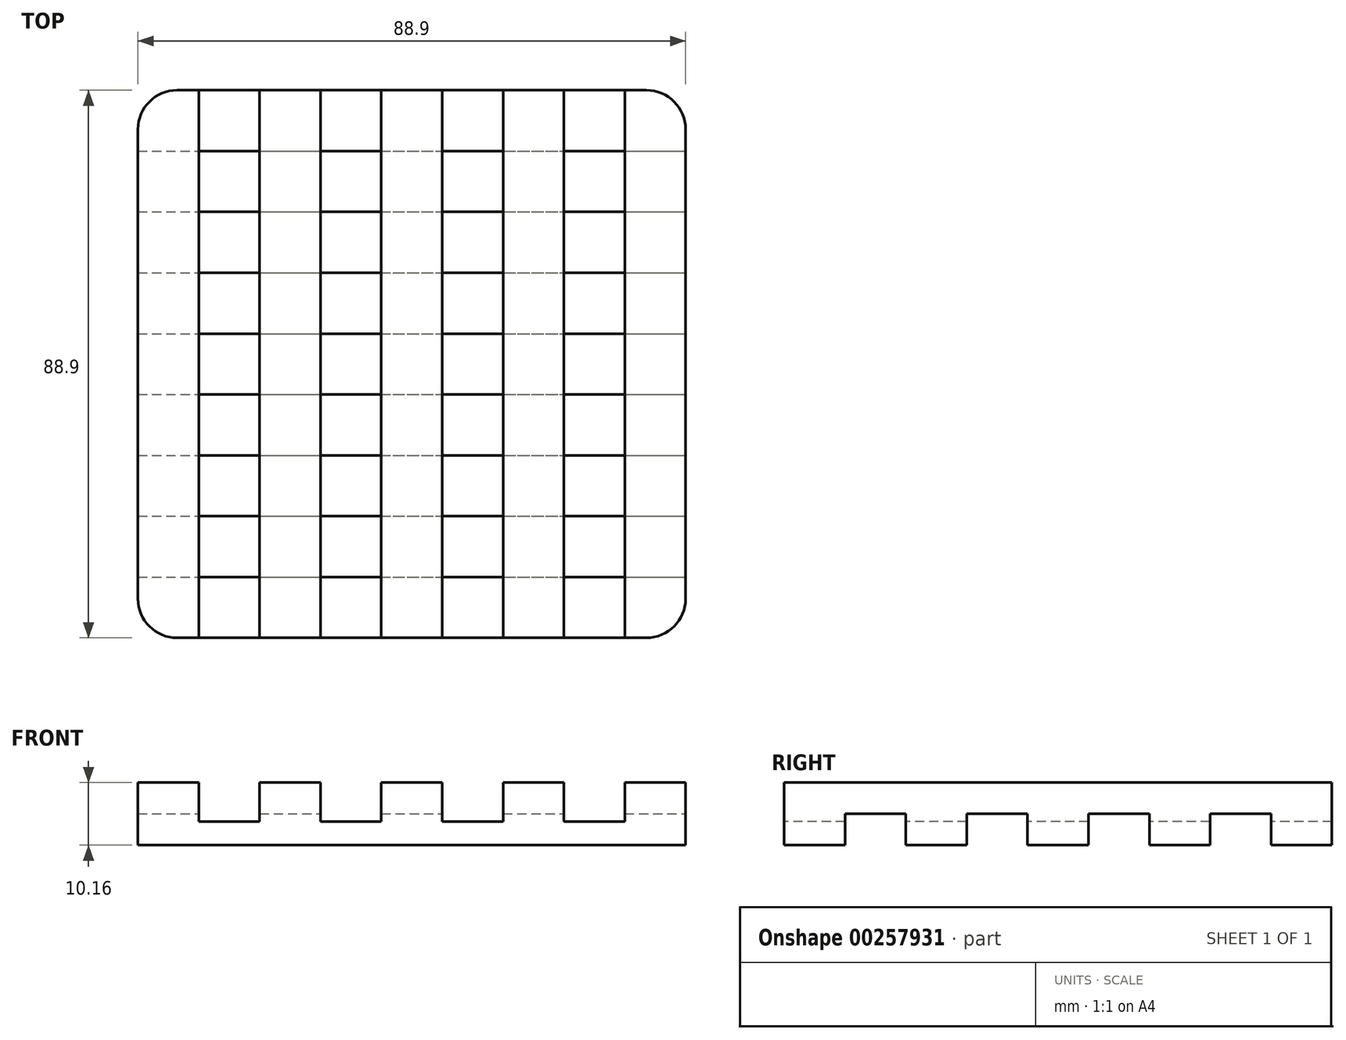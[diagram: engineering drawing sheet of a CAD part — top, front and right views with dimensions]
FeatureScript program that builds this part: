
annotation { "Feature Type Name" : "Feature", "Feature Type Description" : "" }
export const myFeature = defineFeature(function(context is Context, id is Id, definition is map)
    precondition{}
    {
        {
            var Q0;
            Q0=qCreatedBy(makeId("Front.planeOp"),FACE);
            var sketch = newSketch(context, id + "F0", { "sketchPlane" : qUnion([Q0])});
            skLineSegment(sketch, "E0.bottom", {"start": v(44.45, 5.08) * mm, "end": v(-44.45, 5.08) * mm});
            skLineSegment(sketch, "E0.top", {"start": v(44.45, -5.08) * mm, "end": v(-44.45, -5.08) * mm});
            skLineSegment(sketch, "E0.left", {"start": v(44.45, 5.08) * mm, "end": v(44.45, -5.08) * mm});
            skLineSegment(sketch, "E0.right", {"start": v(-44.45, 5.08) * mm, "end": v(-44.45, -5.08) * mm});
            skPoint(sketch, "E0.middle", {"position": v(0, 0) * mm});
            skSolve(sketch);
        }
        {
            var Q0;
            Q0=makeQuery(id+"F0.imprint","IMPRINT",FACE,{"disambiguationData":[TD([[makeQuery(id+"F0.imprint","IMPRINT",EDGE,{"derivedFrom":sQuery(id+"F0.wireOp",EDGE,"E0.bottom")}),1.0]])]});
            extrude(context, id + "F1", {"entities" : qUnion([Q0]), "depth" : 88.9 * mm});
        }
        {
            var Q0;
            Q0=makeQuery(id+"F1.opExtrude","CAP_EDGE",EDGE,{"disambiguationData":[OSD([sQuery(id+"F0.wireOp",EDGE,"E0.right")])],"isStart":false});
            var Q1;
            Q1=makeQuery(id+"F1.opExtrude","CAP_EDGE",EDGE,{"disambiguationData":[OSD([sQuery(id+"F0.wireOp",EDGE,"E0.left")])],"isStart":false});
            var Q2;
            Q2=makeQuery(id+"F1.opExtrude","CAP_EDGE",EDGE,{"disambiguationData":[OSD([sQuery(id+"F0.wireOp",EDGE,"E0.left")])],"isStart":true});
            var Q3;
            Q3=makeQuery(id+"F1.opExtrude","CAP_EDGE",EDGE,{"disambiguationData":[OSD([sQuery(id+"F0.wireOp",EDGE,"E0.right")])],"isStart":true});
            fillet(context, id + "F2", {"entities" : qUnion([Q0, Q1, Q2, Q3]), "radius" : 6.35 * mm, "tangentPropagation" : true, "allowEdgeOverflow" : false});
        }
        {
            var Q0;
            Q0=makeQuery(id+"F1.opExtrude","CAP_FACE",FACE,{"disambiguationData":[OSD([sQuery(id+"F0.wireOp",EDGE,"E0.bottom"),sQuery(id+"F0.wireOp",EDGE,"E0.top"),sQuery(id+"F0.wireOp",EDGE,"E0.left"),sQuery(id+"F0.wireOp",EDGE,"E0.right")])],"isStart":false});
            var sketch = newSketch(context, id + "F3", { "sketchPlane" : qUnion([Q0])});
            skLineSegment(sketch, "E1", {"start": v(-44.45, -1.27) * mm, "end": v(44.45, -1.27) * mm, "construction": true});
            skLineSegment(sketch, "E2.bottom", {"start": v(-34.57, 5.08) * mm, "end": v(-24.7, 5.08) * mm});
            skLineSegment(sketch, "E2.top", {"start": v(-34.57, -1.27) * mm, "end": v(-24.7, -1.27) * mm});
            skLineSegment(sketch, "E2.left", {"start": v(-34.57, 5.08) * mm, "end": v(-34.57, -1.27) * mm});
            skLineSegment(sketch, "E2.right", {"start": v(-24.7, 5.08) * mm, "end": v(-24.7, -1.27) * mm});
            skLineSegment(sketch, "E3.bottom", {"start": v(-14.82, 5.08) * mm, "end": v(-4.94, 5.08) * mm});
            skLineSegment(sketch, "E3.top", {"start": v(-14.82, -1.27) * mm, "end": v(-4.94, -1.27) * mm});
            skLineSegment(sketch, "E3.left", {"start": v(-14.82, 5.08) * mm, "end": v(-14.82, -1.27) * mm});
            skLineSegment(sketch, "E3.right", {"start": v(-4.94, 5.08) * mm, "end": v(-4.94, -1.27) * mm});
            skLineSegment(sketch, "E4.bottom", {"start": v(4.94, 5.08) * mm, "end": v(14.82, 5.08) * mm});
            skLineSegment(sketch, "E4.top", {"start": v(4.94, -1.27) * mm, "end": v(14.82, -1.27) * mm});
            skLineSegment(sketch, "E4.left", {"start": v(4.94, 5.08) * mm, "end": v(4.94, -1.27) * mm});
            skLineSegment(sketch, "E4.right", {"start": v(14.82, 5.08) * mm, "end": v(14.82, -1.27) * mm});
            skLineSegment(sketch, "E5.bottom", {"start": v(24.7, 5.08) * mm, "end": v(34.57, 5.08) * mm});
            skLineSegment(sketch, "E5.top", {"start": v(24.7, -1.27) * mm, "end": v(34.57, -1.27) * mm});
            skLineSegment(sketch, "E5.left", {"start": v(24.7, 5.08) * mm, "end": v(24.7, -1.27) * mm});
            skLineSegment(sketch, "E5.right", {"start": v(34.57, 5.08) * mm, "end": v(34.57, -1.27) * mm});
            skSolve(sketch);
        }
        {
            var Q0;
            Q0=makeQuery(id+"F3.imprint","IMPRINT",FACE,{"disambiguationData":[TD([[makeQuery(id+"F3.imprint","IMPRINT",EDGE,{"derivedFrom":sQuery(id+"F3.wireOp",EDGE,"E2.bottom")}),1.0]])]});
            var Q1;
            Q1=makeQuery(id+"F3.imprint","IMPRINT",FACE,{"disambiguationData":[TD([[makeQuery(id+"F3.imprint","IMPRINT",EDGE,{"derivedFrom":sQuery(id+"F3.wireOp",EDGE,"E3.bottom")}),1.0]])]});
            var Q2;
            Q2=makeQuery(id+"F3.imprint","IMPRINT",FACE,{"disambiguationData":[TD([[makeQuery(id+"F3.imprint","IMPRINT",EDGE,{"derivedFrom":sQuery(id+"F3.wireOp",EDGE,"E4.bottom")}),1.0]])]});
            var Q3;
            Q3=makeQuery(id+"F3.imprint","IMPRINT",FACE,{"disambiguationData":[TD([[makeQuery(id+"F3.imprint","IMPRINT",EDGE,{"derivedFrom":sQuery(id+"F3.wireOp",EDGE,"E5.bottom")}),1.0]])]});
            extrude(context, id + "F4", {"entities" : qUnion([Q0, Q1, Q2, Q3]), "operationType" : NewBodyOperationType.REMOVE, "endBound" : BoundingType.THROUGH_ALL, "oppositeDirection" : true, "depth" : 25.4 * mm});
        }
        {
            var Q0;
            Q0=makeQuery(id+"F1.opExtrude","SWEPT_FACE",FACE,{"disambiguationData":[OSD([sQuery(id+"F0.wireOp",EDGE,"E0.left")])]});
            var sketch = newSketch(context, id + "F5", { "sketchPlane" : qUnion([Q0])});
            skLineSegment(sketch, "E6", {"start": v(-88.9, -5.08) * mm, "end": v(0, -5.08) * mm});
            skLineSegment(sketch, "E7.bottom", {"start": v(-79.02, 0) * mm, "end": v(-69.14, 0) * mm});
            skLineSegment(sketch, "E7.top", {"start": v(-79.02, -5.08) * mm, "end": v(-69.14, -5.08) * mm});
            skLineSegment(sketch, "E7.left", {"start": v(-79.02, 0) * mm, "end": v(-79.02, -5.08) * mm});
            skLineSegment(sketch, "E7.right", {"start": v(-69.14, 0) * mm, "end": v(-69.14, -5.08) * mm});
            skLineSegment(sketch, "E8.bottom", {"start": v(-59.27, 0) * mm, "end": v(-49.39, 0) * mm});
            skLineSegment(sketch, "E8.top", {"start": v(-59.27, -5.08) * mm, "end": v(-49.39, -5.08) * mm});
            skLineSegment(sketch, "E8.left", {"start": v(-59.27, 0) * mm, "end": v(-59.27, -5.08) * mm});
            skLineSegment(sketch, "E8.right", {"start": v(-49.39, 0) * mm, "end": v(-49.39, -5.08) * mm});
            skLineSegment(sketch, "E9.bottom", {"start": v(-39.51, 0) * mm, "end": v(-29.63, 0) * mm});
            skLineSegment(sketch, "E9.top", {"start": v(-39.51, -5.08) * mm, "end": v(-29.63, -5.08) * mm});
            skLineSegment(sketch, "E9.left", {"start": v(-39.51, 0) * mm, "end": v(-39.51, -5.08) * mm});
            skLineSegment(sketch, "E9.right", {"start": v(-29.63, 0) * mm, "end": v(-29.63, -5.08) * mm});
            skLineSegment(sketch, "E10.bottom", {"start": v(-19.76, 0) * mm, "end": v(-9.88, 0) * mm});
            skLineSegment(sketch, "E10.top", {"start": v(-19.76, -5.08) * mm, "end": v(-9.88, -5.08) * mm});
            skLineSegment(sketch, "E10.left", {"start": v(-19.76, 0) * mm, "end": v(-19.76, -5.08) * mm});
            skLineSegment(sketch, "E10.right", {"start": v(-9.88, 0) * mm, "end": v(-9.88, -5.08) * mm});
            skLineSegment(sketch, "E11", {"start": v(0, 0) * mm, "end": v(-88.9, 0) * mm, "construction": true});
            skSolve(sketch);
        }
        {
            var Q0;
            Q0=makeQuery(id+"F5.imprint","IMPRINT",FACE,{"disambiguationData":[TD([[makeQuery(id+"F5.imprint","IMPRINT",EDGE,{"derivedFrom":sQuery(id+"F5.wireOp",EDGE,"E10.bottom")}),-1.0]])]});
            var Q1;
            Q1=makeQuery(id+"F5.imprint","IMPRINT",FACE,{"disambiguationData":[TD([[makeQuery(id+"F5.imprint","IMPRINT",EDGE,{"derivedFrom":sQuery(id+"F5.wireOp",EDGE,"E9.bottom")}),-1.0]])]});
            var Q2;
            Q2=makeQuery(id+"F5.imprint","IMPRINT",FACE,{"disambiguationData":[TD([[makeQuery(id+"F5.imprint","IMPRINT",EDGE,{"derivedFrom":sQuery(id+"F5.wireOp",EDGE,"E8.bottom")}),-1.0]])]});
            var Q3;
            Q3=makeQuery(id+"F5.imprint","IMPRINT",FACE,{"disambiguationData":[TD([[makeQuery(id+"F5.imprint","IMPRINT",EDGE,{"derivedFrom":sQuery(id+"F5.wireOp",EDGE,"E7.bottom")}),-1.0]])]});
            extrude(context, id + "F6", {"entities" : qUnion([Q0, Q1, Q2, Q3]), "operationType" : NewBodyOperationType.REMOVE, "endBound" : BoundingType.THROUGH_ALL, "oppositeDirection" : true, "depth" : 25.4 * mm});
        }
    });
